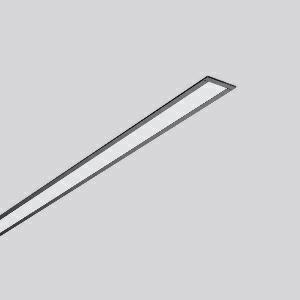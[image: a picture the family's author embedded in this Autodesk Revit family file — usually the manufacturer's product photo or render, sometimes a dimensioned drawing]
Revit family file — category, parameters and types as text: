
# Revit family: less_is_more_27_312178_003_1_463f
name_source: partatom
category: Lighting Fixtures
units: mm (PartAtom-declared; Revit-internal decimal feet)

## family parameters
Cut with Voids When Loaded = No
Host = Face
Light Source = No
Part Type = Normal
Room Calculation Point = No
Round Connector Dimension = Use Diameter
Shared = No

## types (1)
- LESS IS MORE 27 (1 x LED Modul 840, 2400 lm, 4000)
    Apparent Load = 39 VA
    CIE Flux Codes = 48 79 96 100 100
    Color Rendering = 80
    Color Temperature = 4000
    Default Elevation = 1800 mm
    Description = Series: LESS IS MORE 27
Recessed ceiling and wall luminaire with slim design. Housing: extruded aluminium profile, powder-coated. End cap aluminium powder-coated. Diffuser made of non-yellowing plastic (PMMA), opal. Suitable for Recessed ceiling mounting, wall (recessed). External driver with connecting cable. 
Colour: deep black, matt (RAL 9005)
Length: 1514 mm
Width: 38 mm
Height: 2 mm
Cut-out length: 1506 mm
Cut-out width: 30 mm
Recess height: 45-60 mm
Luminaire: recess height: 37 mm
Lamp: LED
Socket: without socket
Colour temperature: 4000K
Colour rendering index (CRI): 82
System power: 39 W
Rated luminous flux: 2400 lm
Luminous efficiency: 62 lm/W
Control gear: Regulated power supply
Protection class: II
Type of protection: IP 20
    Height = 0 mm  [stored 0 ft]
    Lamp = 1 x LED Modul 840
    Lamp Light Flux = 2400 lm
    Lamp count = 1
    Length = 1514 mm
    Lifetime = 50000 h
    Luminous efficacy = 62 lm/W
    Manufacturer = RZB
    ModVariant = No
    Model = 312178.003.1
    Mounting Place = Ceiling, Wall
    Mounting Type = Recessed
    Number of Poles = 1
    OnlyDefault = Yes
    Power Factor = 1
    Product Name = LESS IS MORE 27
    Product group = Recessed LED linear luminaires
    ProductGroupID = 407
    Protection Class = Protection class II
    Protection Degree = IP 20
    RLX_Detail_Level = 1
    RLX_Emergency_Light_Flux = 0 lm
    RLX_Emergency_Type = 0
    RLX_Emergency_Type_DB = No
    RlxData = <blob elided: 26129 chars, md5=d44b1ecd>
    Socket = socket
    Standby Power = 0 W
    System Light Flux = 2400 lm
    System Power = 39 W
    Type Comments = Product without accessories
    Type Image = 312176.003.jpg
    URL = http://relux.com
    VarID = ---
    Voltage = 230 V
    Voltage Range = 220-240 V
    Weight = 0.00 kg
    Width = 38 mm

note: [stored X ft] marks values corroborated as IEEE doubles in the binary element streams (Revit-internal decimal feet)

## geometry (parser evidence)
native form markers: Blend x4, Sweep x11
no freeform markers — native parametric forms only
